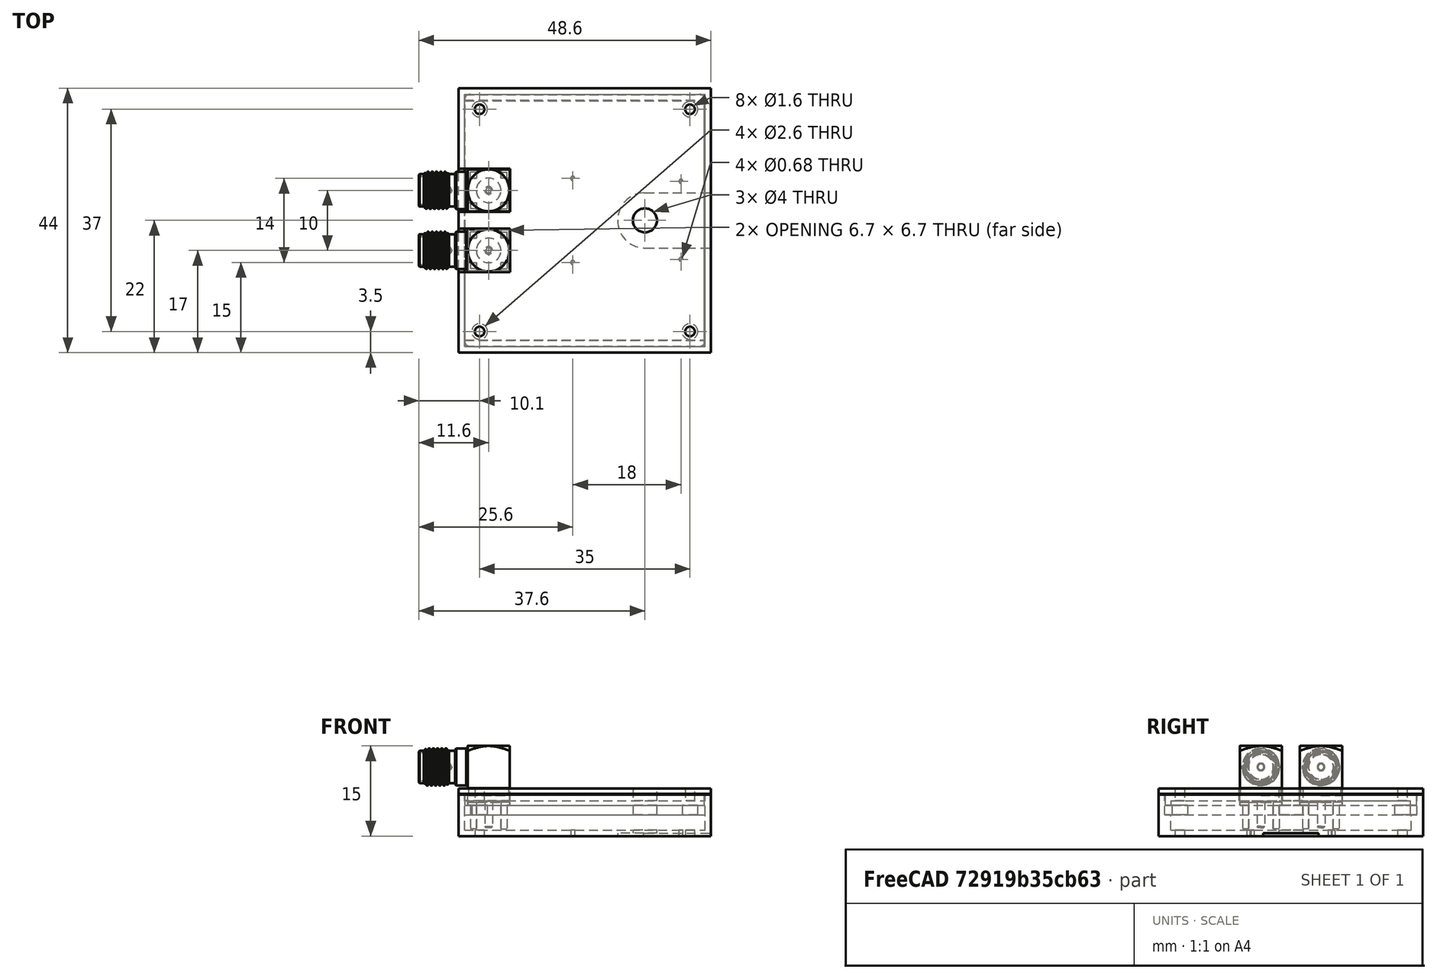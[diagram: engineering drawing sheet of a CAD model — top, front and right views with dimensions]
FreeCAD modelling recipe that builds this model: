
FCSTD DOCUMENT  (FreeCAD 0.21R33675 (Git))
Label: ModulationKickerHousing
License: All rights reserved
LicenseURL: http://en.wikipedia.org/wiki/All_rights_reserved
objects: TechDraw::DrawViewDimension×52, Part::Cylinder×21, Part::Box×12, Part::Cut×11, TechDraw::DrawProjGroupItem×9, Part::Compound×8, Part::MultiFuse×4, TechDraw::DrawSVGTemplate×3, TechDraw::DrawProjGroup×3, TechDraw::DrawPage×3, Part::Feature×2, TechDraw::DrawViewSection×2, App::Link×1, Part::Fillet×1
note: 151 computed .brp shape members not serialized (recipe doc carries the construction recipe); baked Part::Feature solids carry a one-line shape summary decoded from their .brp
EXTERNAL_REF file=../../PhilipsXL30/XL30FinalAppertureHolder.FCStd obj=Cut001_solid

FEATURE [Part::Box] Box  label="Würfel"
  AttacherType = Attacher::AttachEngine3D
  Height = 1.6
  Length = 40
  Width = 42
FEATURE [Part::Feature] Solid  label="901-143-6RFX"
  Placement = pos=(0,0,0) rot=(-1,0,0;1.5708rad)
  shape: bbox 16.55 x 9.9 x 13.8 mm, 108 faces (baked)
FEATURE [Part::Compound] Compound
  Links = -> [Solid]
  Placement = pos=(4,16,8) rot=(0,0,1;3.14159rad)
FEATURE [Part::Cylinder] Cylinder  label="Zylinder"
  Angle = 360
  AttacherType = Attacher::AttachEngine3D
  FirstAngle = 0
  Height = 5
  Placement = pos=(30,21,0) rot=(0,0,1;0rad)
  Radius = 2
  SecondAngle = 0
FEATURE [Part::Cut] Cut
  Base = -> Box
  Tool = -> Cylinder
FEATURE [Part::Box] Box001  label="Würfel001"
  AttacherType = Attacher::AttachEngine3D
  Height = 7
  Length = 42
  Placement = pos=(-1,-1,-4.4) rot=(0,0,1;0rad)
  Width = 44
FEATURE [Part::Box] Box002  label="Würfel002"
  AttacherType = Attacher::AttachEngine3D
  Height = 6
  Length = 40
  Placement = pos=(0,0,-3.4) rot=(0,0,1;0rad)
  Width = 42
FEATURE [Part::Cut] Cut001
  Base = -> Box001
  Tool = -> Box002
FEATURE [Part::Cylinder] Cylinder001  label="Zylinder001"
  Angle = 360
  AttacherType = Attacher::AttachEngine3D
  FirstAngle = 0
  Height = 20
  Placement = pos=(30,21,-10) rot=(0,0,1;0rad)
  Radius = 2
  SecondAngle = 0
FEATURE [Part::Cut] Cut002
  Base = -> Cut001
  Tool = -> Cylinder001
FEATURE [Part::Box] Box003  label="Würfel003"
  AttacherType = Attacher::AttachEngine3D
  Height = 2.5
  Length = 40
  Placement = pos=(0,0,-3.4) rot=(0,0,1;0rad)
  Width = 1
FEATURE [Part::Box] Box004  label="Würfel004"
  AttacherType = Attacher::AttachEngine3D
  Height = 2.5
  Length = 40
  Placement = pos=(0,41,-3.4) rot=(0,0,1;0rad)
  Width = 1
FEATURE [Part::MultiFuse] Fusion
  Shapes = -> [Box003,Box004,Cut002]
FEATURE [Part::Box] Box005  label="Würfel005"
  AttacherType = Attacher::AttachEngine3D
  Height = 1
  Length = 39.8
  Placement = pos=(0.1,0.1,1.5) rot=(0,0,1;0rad)
  Width = 41.8
FEATURE [Part::Box] Box006  label="Würfel006"
  AttacherType = Attacher::AttachEngine3D
  Height = 1
  Length = 42
  Placement = pos=(-1,-1,2.5) rot=(0,0,1;0rad)
  Width = 44
FEATURE [Part::MultiFuse] Fusion001
  Shapes = -> [Box005,Box006]
FEATURE [Part::Box] Box007  label="Würfel007"
  AttacherType = Attacher::AttachEngine3D
  Height = 10
  Length = 20
  Placement = pos=(-12.4,12.4,0) rot=(0,0,1;0rad)
  Width = 7.2
FEATURE [Part::Cut] Cut003
  Base = -> Fusion001
  Tool = -> Box007
FEATURE [Part::Box] Box008  label="Würfel008"
  AttacherType = Attacher::AttachEngine3D
  Height = 0.5
  Length = 18
  Placement = pos=(27.5,16.4,-4.4) rot=(0,0,1;0rad)
  Width = 9.2
FEATURE [Part::Cylinder] Cylinder002  label="Zylinder002"
  Angle = 360
  AttacherType = Attacher::AttachEngine3D
  FirstAngle = 0
  Height = 0.5
  Placement = pos=(27.75,21,-4.4) rot=(0,0,1;0rad)
  Radius = 4.6
  SecondAngle = 0
FEATURE [Part::Cylinder] Cylinder003  label="Zylinder003"
  Angle = 360
  AttacherType = Attacher::AttachEngine3D
  FirstAngle = 0
  Height = 0.5
  Placement = pos=(27.75,21,-4.4) rot=(0,0,1;0rad)
  Radius = 4.6
  SecondAngle = 0
FEATURE [Part::MultiFuse] Fusion002
  Placement = pos=(2.3,0,0) rot=(0,0,1;0rad)
  Shapes = -> [Box008,Cylinder002,Cylinder003]
FEATURE [Part::Cut] Cut004
  Base = -> Fusion
  Tool = -> Fusion002
FEATURE [Part::Cylinder] Cylinder004  label="Zylinder004"
  Angle = 360
  AttacherType = Attacher::AttachEngine3D
  FirstAngle = 0
  Height = 100
  Placement = pos=(18,14,-50) rot=(0,0,1;0rad)
  Radius = 0.34
  SecondAngle = 0
FEATURE [Part::Cylinder] Cylinder005  label="Zylinder005"
  Angle = 360
  AttacherType = Attacher::AttachEngine3D
  FirstAngle = 0
  Height = 100
  Placement = pos=(18,28,-50) rot=(0,0,1;0rad)
  Radius = 0.34
  SecondAngle = 0
FEATURE [Part::Cylinder] Cylinder006  label="Zylinder006"
  Angle = 360
  AttacherType = Attacher::AttachEngine3D
  FirstAngle = 0
  Height = 100
  Placement = pos=(36,14.5,-50) rot=(0,0,1;0rad)
  Radius = 0.34
  SecondAngle = 0
FEATURE [Part::Cylinder] Cylinder007  label="Zylinder007"
  Angle = 360
  AttacherType = Attacher::AttachEngine3D
  FirstAngle = 0
  Height = 100
  Placement = pos=(36,27.5,-50) rot=(0,0,1;0rad)
  Radius = 0.34
  SecondAngle = 0
FEATURE [Part::Compound] Compound002  label="M1TapHoles"
  Links = -> [Cylinder004,Cylinder005,Cylinder006,Cylinder007]
FEATURE [Part::Cut] Cut005
  Base = -> Cut004
  Tool = -> Compound002
FEATURE [Part::Box] Box009  label="Würfel009"
  AttacherType = Attacher::AttachEngine3D
  Height = 0.8
  Length = 39.8
  Placement = pos=(0.1,40.9,0.7) rot=(0,0,1;0rad)
  Width = 1
FEATURE [Part::Box] Box010  label="Würfel010"
  AttacherType = Attacher::AttachEngine3D
  Height = 0.8
  Length = 39.8
  Placement = pos=(0.1,0.1,0.7) rot=(0,0,1;0rad)
  Width = 1
FEATURE [Part::Compound] Compound003
  Links = -> [Box009,Box010]
FEATURE [Part::MultiFuse] Fusion003
  Shapes = -> [Cut003,Compound003]
FEATURE [Part::Cylinder] Cylinder008  label="Zylinder008"
  Angle = 360
  AttacherType = Attacher::AttachEngine3D
  FirstAngle = 0
  Height = 20
  Placement = pos=(37.5,2.5,-10) rot=(0,0,1;0rad)
  Radius = 0.8
  SecondAngle = 0
FEATURE [Part::Cylinder] Cylinder009  label="Zylinder009"
  Angle = 360
  AttacherType = Attacher::AttachEngine3D
  FirstAngle = 0
  Height = 20
  Placement = pos=(2.5,2.5,-10) rot=(0,0,1;0rad)
  Radius = 0.8
  SecondAngle = 0
FEATURE [Part::Cylinder] Cylinder010  label="Zylinder010"
  Angle = 360
  AttacherType = Attacher::AttachEngine3D
  FirstAngle = 0
  Height = 20
  Placement = pos=(37.5,39.5,-10) rot=(0,0,1;0rad)
  Radius = 0.8
  SecondAngle = 0
FEATURE [Part::Cylinder] Cylinder011  label="Zylinder011"
  Angle = 360
  AttacherType = Attacher::AttachEngine3D
  FirstAngle = 0
  Height = 20
  Placement = pos=(2.5,39.5,-10) rot=(0,0,1;0rad)
  Radius = 0.8
  SecondAngle = 0
FEATURE [Part::Cylinder] Cylinder012  label="Zylinder012"
  Angle = 360
  AttacherType = Attacher::AttachEngine3D
  FirstAngle = 0
  Height = 20
  Placement = pos=(37.5,2.5,-10) rot=(0,0,1;0rad)
  Radius = 1.3
  SecondAngle = 0
FEATURE [Part::Cylinder] Cylinder013  label="Zylinder013"
  Angle = 360
  AttacherType = Attacher::AttachEngine3D
  FirstAngle = 0
  Height = 20
  Placement = pos=(2.5,2.5,-10) rot=(0,0,1;0rad)
  Radius = 1.3
  SecondAngle = 0
FEATURE [Part::Cylinder] Cylinder014  label="Zylinder014"
  Angle = 360
  AttacherType = Attacher::AttachEngine3D
  FirstAngle = 0
  Height = 20
  Placement = pos=(37.5,39.5,-10) rot=(0,0,1;0rad)
  Radius = 1.3
  SecondAngle = 0
FEATURE [Part::Cylinder] Cylinder015  label="Zylinder015"
  Angle = 360
  AttacherType = Attacher::AttachEngine3D
  FirstAngle = 0
  Height = 20
  Placement = pos=(2.5,39.5,-10) rot=(0,0,1;0rad)
  Radius = 1.3
  SecondAngle = 0
FEATURE [Part::Compound] Compound004
  Links = -> [Cylinder015,Cylinder012,Cylinder013,Cylinder014]
FEATURE [Part::Cylinder] Cylinder016  label="Zylinder016"
  Angle = 360
  AttacherType = Attacher::AttachEngine3D
  FirstAngle = 0
  Height = 20
  Placement = pos=(37.5,2.5,-10) rot=(0,0,1;0rad)
  Radius = 0.8
  SecondAngle = 0
FEATURE [Part::Cylinder] Cylinder017  label="Zylinder017"
  Angle = 360
  AttacherType = Attacher::AttachEngine3D
  FirstAngle = 0
  Height = 20
  Placement = pos=(2.5,2.5,-10) rot=(0,0,1;0rad)
  Radius = 0.8
  SecondAngle = 0
FEATURE [Part::Cylinder] Cylinder018  label="Zylinder018"
  Angle = 360
  AttacherType = Attacher::AttachEngine3D
  FirstAngle = 0
  Height = 20
  Placement = pos=(37.5,39.5,-10) rot=(0,0,1;0rad)
  Radius = 0.8
  SecondAngle = 0
FEATURE [Part::Cylinder] Cylinder019  label="Zylinder019"
  Angle = 360
  AttacherType = Attacher::AttachEngine3D
  FirstAngle = 0
  Height = 20
  Placement = pos=(2.5,39.5,-10) rot=(0,0,1;0rad)
  Radius = 0.8
  SecondAngle = 0
FEATURE [Part::Compound] Compound005
  Links = -> [Cylinder008,Cylinder009,Cylinder010,Cylinder011]
FEATURE [Part::Cut] Cut007  label="UpperPart"
  Base = -> Cut005
  Tool = -> Compound005
FEATURE [Part::Compound] Compound006
  Links = -> [Cylinder019,Cylinder016,Cylinder017,Cylinder018]
FEATURE [Part::Cut] Cut008  label="LowerPart"
  Base = -> Fusion003
  Tool = -> Compound006
FEATURE [App::Link] Link  label="XL30FinalAppertureHolder"
  LinkPlacement = pos=(30,21,-4) rot=(1,0,0;3.14159rad)
  LinkedObject = -> <external ../../PhilipsXL30/XL30FinalAppertureHolder.FCStd>#Cut001_solid
  Placement = pos=(30,21,-4) rot=(1,0,0;3.14159rad)
FEATURE [TechDraw::DrawSVGTemplate] Template
  EditableTexts = Designed_by_Name=Thomas Spielauer; FC-Date=2023-10-02; FC-SC=mm; FC-SH=1/3; FC-Title=SemKicker Housing v2; Subtitle=Version 2, Lower Part, Dual Port
  Height = 210
  Orientation = 1
  Template = <path>
  Width = 297
FEATURE [TechDraw::DrawProjGroupItem] ProjItem  label="Front"
  CoarseView = false
  Direction = (0,0,-1)
  Focus = 100
  HardHidden = false
  IsoCount = 0
  IsoHidden = false
  IsoVisible = false
  LockPosition = true
  Perspective = false
  Rotation = 0
  RotationVector = (0,1,0)
  ScaleType = 2
  ScrubCount = 0
  SeamHidden = false
  SeamVisible = false
  SmoothHidden = false
  SmoothVisible = true
  Source = -> [Cut007]
  Type = 0
  X = 0
  XDirection = (0,1,0)
  Y = 0
FEATURE [TechDraw::DrawProjGroupItem] ProjItem001  label="Left"
  CoarseView = false
  Direction = (0,-1,-1e-16)
  Focus = 100
  HardHidden = false
  IsoCount = 0
  IsoHidden = false
  IsoVisible = false
  LockPosition = false
  Perspective = false
  Rotation = 0
  RotationVector = (1,0,0)
  ScaleType = 2
  ScrubCount = 0
  SeamHidden = false
  SeamVisible = false
  SmoothHidden = false
  SmoothVisible = true
  Source = -> [Cut007]
  Type = 1
  X = 55.0312
  XDirection = (0,1e-16,-1)
  Y = 0
FEATURE [TechDraw::DrawProjGroupItem] ProjItem002  label="Top"
  CoarseView = false
  Direction = (1,0,0)
  Focus = 100
  HardHidden = false
  IsoCount = 0
  IsoHidden = false
  IsoVisible = false
  LockPosition = false
  Perspective = false
  Rotation = 0
  RotationVector = (1,0,0)
  ScaleType = 2
  ScrubCount = 0
  SeamHidden = false
  SeamVisible = false
  SmoothHidden = false
  SmoothVisible = true
  Source = -> [Cut007]
  Type = 4
  X = 0
  XDirection = (0,1,0)
  Y = -63.5568
FEATURE [TechDraw::DrawProjGroupItem] ProjItem003  label="FrontTopLeft"
  CoarseView = false
  Direction = (0.57735,-0.57735,-0.57735)
  Focus = 100
  HardHidden = false
  IsoCount = 0
  IsoHidden = false
  IsoVisible = false
  LockPosition = false
  Perspective = false
  Rotation = 0
  RotationVector = (1,0,0)
  ScaleType = 2
  ScrubCount = 0
  SeamHidden = false
  SeamVisible = false
  SmoothHidden = false
  SmoothVisible = true
  Source = -> [Cut007]
  Type = 6
  X = 55.0312
  XDirection = (0,0.707107,-0.707107)
  Y = -63.5568
FEATURE [TechDraw::DrawProjGroup] ProjGroup
  Anchor = -> ProjItem
  AutoDistribute = true
  LockPosition = false
  ProjectionType = 0
  Rotation = 0
  ScaleType = 0
  Source = -> [Cut007]
  Views = -> [ProjItem,ProjItem001,ProjItem002,ProjItem003]
  X = 55.1699
  Y = 140.445
  spacingX = 15
  spacingY = 15
FEATURE [TechDraw::DrawViewDimension] Dimension
  AngleOverride = false
  Arbitrary = false
  ArbitraryTolerances = false
  EqualTolerance = true
  ExtensionAngle = 0
  FormatSpec = %.2w
  FormatSpecOverTolerance = %+.2w
  FormatSpecUnderTolerance = %+.2w
  Inverted = false
  LineAngle = 0
  LockPosition = false
  MeasureType = 1
  OverTolerance = 0
  References2D = -> [ProjItem]
  Rotation = 0
  ScaleType = 0
  TheoreticalExact = false
  Type = 1
  UnderTolerance = 0
  X = 1.25393
  Y = -36.4347
FEATURE [TechDraw::DrawViewDimension] Dimension001
  AngleOverride = false
  Arbitrary = false
  ArbitraryTolerances = false
  EqualTolerance = true
  ExtensionAngle = 0
  FormatSpec = %.2w
  FormatSpecOverTolerance = %+.2w
  FormatSpecUnderTolerance = %+.2w
  Inverted = false
  LineAngle = 0
  LockPosition = false
  MeasureType = 1
  OverTolerance = 0
  References2D = -> [ProjItem]
  Rotation = 0
  ScaleType = 0
  TheoreticalExact = false
  Type = 1
  UnderTolerance = 0
  X = -0.666797
  Y = 33.2207
FEATURE [TechDraw::DrawViewDimension] Dimension002
  AngleOverride = false
  Arbitrary = false
  ArbitraryTolerances = false
  EqualTolerance = true
  ExtensionAngle = 0
  FormatSpec = ⌀%.2w
  FormatSpecOverTolerance = %+.2w
  FormatSpecUnderTolerance = %+.2w
  Inverted = false
  LineAngle = 0
  LockPosition = false
  MeasureType = 1
  OverTolerance = 0
  References2D = -> [ProjItem]
  Rotation = 0
  ScaleType = 0
  TheoreticalExact = false
  Type = 5
  UnderTolerance = 0
  X = 28.4277
  Y = 10.052
FEATURE [TechDraw::DrawViewDimension] Dimension003
  AngleOverride = false
  Arbitrary = false
  ArbitraryTolerances = false
  EqualTolerance = true
  ExtensionAngle = 0
  FormatSpec = %.2w
  FormatSpecOverTolerance = %+.2w
  FormatSpecUnderTolerance = %+.2w
  Inverted = false
  LineAngle = 0
  LockPosition = false
  MeasureType = 1
  OverTolerance = 0
  References2D = -> [ProjItem]
  Rotation = 0
  ScaleType = 0
  TheoreticalExact = false
  Type = 1
  UnderTolerance = 0
  X = -29.3827
  Y = 33.2539
FEATURE [TechDraw::DrawViewDimension] Dimension004
  AngleOverride = false
  Arbitrary = false
  ArbitraryTolerances = false
  EqualTolerance = true
  ExtensionAngle = 0
  FormatSpec = %.2w
  FormatSpecOverTolerance = %+.2w
  FormatSpecUnderTolerance = %+.2w
  Inverted = false
  LineAngle = 0
  LockPosition = false
  MeasureType = 1
  OverTolerance = 0
  References2D = -> [ProjItem]
  Rotation = 0
  ScaleType = 0
  TheoreticalExact = false
  Type = 0
  UnderTolerance = 0
  X = 20.6616
  Y = 33.2266
FEATURE [TechDraw::DrawViewDimension] Dimension005
  AngleOverride = false
  Arbitrary = false
  ArbitraryTolerances = false
  EqualTolerance = true
  ExtensionAngle = 0
  FormatSpec = %.2w
  FormatSpecOverTolerance = %+.2w
  FormatSpecUnderTolerance = %+.2w
  Inverted = false
  LineAngle = 0
  LockPosition = false
  MeasureType = 1
  OverTolerance = 0
  References2D = -> [ProjItem]
  Rotation = 0
  ScaleType = 0
  TheoreticalExact = false
  Type = 2
  UnderTolerance = 0
  X = -39.0583
  Y = 14.7874
FEATURE [TechDraw::DrawViewDimension] Dimension006
  AngleOverride = false
  Arbitrary = false
  ArbitraryTolerances = false
  EqualTolerance = true
  ExtensionAngle = 0
  FormatSpec = %.2w
  FormatSpecOverTolerance = %+.2w
  FormatSpecUnderTolerance = %+.2w
  Inverted = false
  LineAngle = 0
  LockPosition = false
  MeasureType = 1
  OverTolerance = 0
  References2D = -> [ProjItem]
  Rotation = 0
  ScaleType = 0
  TheoreticalExact = false
  Type = 1
  UnderTolerance = 0
  X = -15.1318
  Y = 48.9061
FEATURE [TechDraw::DrawViewDimension] Dimension007
  AngleOverride = false
  Arbitrary = false
  ArbitraryTolerances = false
  EqualTolerance = true
  ExtensionAngle = 0
  FormatSpec = %.2w
  FormatSpecOverTolerance = %+.2w
  FormatSpecUnderTolerance = %+.2w
  Inverted = false
  LineAngle = 0
  LockPosition = false
  MeasureType = 1
  OverTolerance = 0
  References2D = -> [ProjItem]
  Rotation = 0
  ScaleType = 0
  TheoreticalExact = false
  Type = 1
  UnderTolerance = 0
  X = 13.258
  Y = 44.6428
FEATURE [TechDraw::DrawViewDimension] Dimension008
  AngleOverride = false
  Arbitrary = false
  ArbitraryTolerances = false
  EqualTolerance = true
  ExtensionAngle = 0
  FormatSpec = %.2w
  FormatSpecOverTolerance = %+.2w
  FormatSpecUnderTolerance = %+.2w
  Inverted = false
  LineAngle = 0
  LockPosition = false
  MeasureType = 1
  OverTolerance = 0
  References2D = -> [ProjItem]
  Rotation = 0
  ScaleType = 0
  TheoreticalExact = false
  Type = 2
  UnderTolerance = 0
  X = 29.2563
  Y = 26.6245
FEATURE [TechDraw::DrawViewDimension] Dimension009
  AngleOverride = false
  Arbitrary = false
  ArbitraryTolerances = false
  EqualTolerance = true
  ExtensionAngle = 0
  FormatSpec = ⌀%.2w (4x M2)
  FormatSpecOverTolerance = %+.2w
  FormatSpecUnderTolerance = %+.2w
  Inverted = false
  LineAngle = 0
  LockPosition = false
  MeasureType = 1
  OverTolerance = 0
  References2D = -> [ProjItem]
  Rotation = 0
  ScaleType = 0
  TheoreticalExact = false
  Type = 5
  UnderTolerance = 0
  X = 60.575
  Y = 34.3091
FEATURE [TechDraw::DrawViewDimension] Dimension010
  AngleOverride = false
  Arbitrary = false
  ArbitraryTolerances = false
  EqualTolerance = true
  ExtensionAngle = 0
  FormatSpec = %.2w
  FormatSpecOverTolerance = %+.2w
  FormatSpecUnderTolerance = %+.2w
  Inverted = false
  LineAngle = 0
  LockPosition = false
  MeasureType = 1
  OverTolerance = 0
  References2D = -> [ProjItem]
  Rotation = 0
  ScaleType = 0
  TheoreticalExact = false
  Type = 2
  UnderTolerance = 0
  X = -33.5126
  Y = 2.06556
FEATURE [TechDraw::DrawViewDimension] Dimension011
  AngleOverride = false
  Arbitrary = false
  ArbitraryTolerances = false
  EqualTolerance = true
  ExtensionAngle = 0
  FormatSpec = %.2w
  FormatSpecOverTolerance = %+.2w
  FormatSpecUnderTolerance = %+.2w
  Inverted = false
  LineAngle = 0
  LockPosition = false
  MeasureType = 1
  OverTolerance = 0
  References2D = -> [ProjItem]
  Rotation = 0
  ScaleType = 0
  TheoreticalExact = false
  Type = 2
  UnderTolerance = 0
  X = 27.8187
  Y = -8.37147
FEATURE [TechDraw::DrawViewDimension] Dimension012
  AngleOverride = false
  Arbitrary = false
  ArbitraryTolerances = false
  EqualTolerance = true
  ExtensionAngle = 0
  FormatSpec = %.2w
  FormatSpecOverTolerance = %+.2w
  FormatSpecUnderTolerance = %+.2w
  Inverted = false
  LineAngle = 0
  LockPosition = false
  MeasureType = 1
  OverTolerance = 0
  References2D = -> [ProjItem]
  Rotation = 0
  ScaleType = 0
  TheoreticalExact = false
  Type = 2
  UnderTolerance = 0
  X = 45.3481
  Y = -9.26073
FEATURE [TechDraw::DrawViewDimension] Dimension013
  AngleOverride = false
  Arbitrary = false
  ArbitraryTolerances = false
  EqualTolerance = true
  ExtensionAngle = 0
  FormatSpec = %.2w
  FormatSpecOverTolerance = %+.2w
  FormatSpecUnderTolerance = %+.2w
  Inverted = false
  LineAngle = 0
  LockPosition = false
  MeasureType = 1
  OverTolerance = 0
  References2D = -> [ProjItem]
  Rotation = 0
  ScaleType = 0
  TheoreticalExact = false
  Type = 1
  UnderTolerance = 0
  X = 35.7665
  Y = -22.6841
FEATURE [TechDraw::DrawViewDimension] Dimension014
  AngleOverride = false
  Arbitrary = false
  ArbitraryTolerances = false
  EqualTolerance = true
  ExtensionAngle = 0
  FormatSpec = %.2w
  FormatSpecOverTolerance = %+.2w
  FormatSpecUnderTolerance = %+.2w
  Inverted = false
  LineAngle = 0
  LockPosition = false
  MeasureType = 1
  OverTolerance = 0
  References2D = -> [ProjItem]
  Rotation = 0
  ScaleType = 0
  TheoreticalExact = false
  Type = 1
  UnderTolerance = 0
  X = 9.78618
  Y = -21.3047
FEATURE [TechDraw::DrawViewDimension] Dimension015
  AngleOverride = false
  Arbitrary = false
  ArbitraryTolerances = false
  EqualTolerance = true
  ExtensionAngle = 0
  FormatSpec = %.2w
  FormatSpecOverTolerance = %+.2w
  FormatSpecUnderTolerance = %+.2w
  Inverted = false
  LineAngle = 0
  LockPosition = false
  MeasureType = 1
  OverTolerance = 0
  References2D = -> [ProjItem001]
  Rotation = 0
  ScaleType = 0
  TheoreticalExact = false
  Type = 1
  UnderTolerance = 0
  X = 8.50538
  Y = 32.6804
FEATURE [TechDraw::DrawViewDimension] Dimension016
  AngleOverride = false
  Arbitrary = false
  ArbitraryTolerances = false
  EqualTolerance = true
  ExtensionAngle = 0
  FormatSpec = %.2w
  FormatSpecOverTolerance = %+.2w
  FormatSpecUnderTolerance = %+.2w
  Inverted = false
  LineAngle = 0
  LockPosition = false
  MeasureType = 1
  OverTolerance = 0
  References2D = -> [ProjItem002]
  Rotation = 0
  ScaleType = 0
  TheoreticalExact = false
  Type = 2
  UnderTolerance = 0
  X = -33.4894
  Y = 14.4313
FEATURE [TechDraw::DrawViewDimension] Dimension017
  AngleOverride = false
  Arbitrary = false
  ArbitraryTolerances = false
  EqualTolerance = true
  ExtensionAngle = 0
  FormatSpec = %.2w
  FormatSpecOverTolerance = %+.2w
  FormatSpecUnderTolerance = %+.2w
  Inverted = false
  LineAngle = 0
  LockPosition = false
  MeasureType = 1
  OverTolerance = 0
  References2D = -> [ProjItem002]
  Rotation = 0
  ScaleType = 0
  TheoreticalExact = false
  Type = 2
  UnderTolerance = 0
  X = 22.4587
  Y = -6.89394
FEATURE [TechDraw::DrawPage] Page
  KeepUpdated = true
  NextBalloonIndex = 1
  ProjectionType = 0
  Template = -> Template
  Views = -> [ProjGroup,Dimension,Dimension001,Dimension002,Dimension003,Dimension004,Dimension005,Dimension006,Dimension007,Dimension008,Dimension009,Dimension010,Dimension011,Dimension012,Dimension013,Dimension014,Dimension015,Dimension016,Dimension017]
FEATURE [TechDraw::DrawSVGTemplate] Template001
  EditableTexts = Designed_by_Name=Thomas Spielauer; FC-Date=2023-10-02; FC-SC=mm; FC-SH=2/3; FC-Title=SemKicker Housing v2; Subtitle=Version 2, Lower Part, Dual Port
  Height = 210
  Orientation = 1
  Template = <path>
  Width = 297
FEATURE [TechDraw::DrawProjGroupItem] ProjItem004  label="Front001"
  CoarseView = false
  Direction = (0,0,-1)
  Focus = 100
  HardHidden = false
  IsoCount = 0
  IsoHidden = false
  IsoVisible = false
  LockPosition = true
  Perspective = false
  Rotation = 0
  RotationVector = (0,1,0)
  ScaleType = 2
  ScrubCount = 0
  SeamHidden = false
  SeamVisible = false
  SmoothHidden = false
  SmoothVisible = true
  Source = -> [Cut007]
  Type = 0
  X = 0
  XDirection = (0,1,0)
  Y = 0
FEATURE [TechDraw::DrawProjGroup] ProjGroup001
  Anchor = -> ProjItem004
  AutoDistribute = true
  LockPosition = false
  ProjectionType = 0
  Rotation = 0
  ScaleType = 0
  Source = -> [Cut007]
  Views = -> [ProjItem004]
  X = 67.5139
  Y = 171.126
  spacingX = 15
  spacingY = 15
FEATURE [TechDraw::DrawViewSection] SectionView  label="Section  - "
  BaseView = -> ProjItem004
  CoarseView = false
  CutSurfaceDisplay = 2
  Direction = (1,1e-16,0)
  FileGeomPattern = <path>
  FileHatchPattern = <path>
  Focus = 100
  FuseBeforeCut = false
  HardHidden = false
  HatchOffset = (0,0,0)
  HatchRotation = 0
  HatchScale = 1
  IsoCount = 0
  IsoHidden = false
  IsoVisible = false
  LockPosition = false
  NameGeomPattern = Diamant
  Perspective = false
  Rotation = 0
  Scale = 5
  ScaleType = 1
  ScrubCount = 0
  SeamHidden = false
  SeamVisible = false
  SectionDirection = 4
  SectionNormal = (1,1e-16,0)
  SectionOrigin = (20,21,-0.9)
  SmoothHidden = false
  SmoothVisible = true
  Source = -> [Cut007]
  TrimAfterCut = false
  X = 152.009
  XDirection = (-1e-16,1,0)
  Y = 85.8328
FEATURE [TechDraw::DrawViewDimension] Dimension018
  AngleOverride = false
  Arbitrary = false
  ArbitraryTolerances = false
  EqualTolerance = true
  ExtensionAngle = 0
  FormatSpec = %.2w
  FormatSpecOverTolerance = %+.2w
  FormatSpecUnderTolerance = %+.2w
  Inverted = false
  LineAngle = 0
  LockPosition = false
  MeasureType = 1
  OverTolerance = 0
  References2D = -> [SectionView]
  Rotation = 0
  ScaleType = 0
  TheoreticalExact = false
  Type = 0
  UnderTolerance = 0
  X = 4.24631
  Y = 33.9522
FEATURE [TechDraw::DrawViewDimension] Dimension019
  AngleOverride = false
  Arbitrary = false
  ArbitraryTolerances = false
  EqualTolerance = true
  ExtensionAngle = 0
  FormatSpec = %.2w
  FormatSpecOverTolerance = %+.2w
  FormatSpecUnderTolerance = %+.2w
  Inverted = false
  LineAngle = 0
  LockPosition = false
  MeasureType = 1
  OverTolerance = 0
  References2D = -> [SectionView]
  Rotation = 0
  ScaleType = 0
  TheoreticalExact = false
  Type = 1
  UnderTolerance = 0
  X = 4.11387
  Y = 41.9407
FEATURE [TechDraw::DrawViewDimension] Dimension020
  AngleOverride = false
  Arbitrary = false
  ArbitraryTolerances = false
  EqualTolerance = true
  ExtensionAngle = 0
  FormatSpec = %.2w
  FormatSpecOverTolerance = %+.2w
  FormatSpecUnderTolerance = %+.2w
  Inverted = false
  LineAngle = 0
  LockPosition = false
  MeasureType = 1
  OverTolerance = 0
  References2D = -> [SectionView]
  Rotation = 0
  ScaleType = 0
  TheoreticalExact = false
  Type = 1
  UnderTolerance = 0
  X = 3.83962
  Y = 50.2209
FEATURE [TechDraw::DrawViewDimension] Dimension021
  AngleOverride = false
  Arbitrary = false
  ArbitraryTolerances = false
  EqualTolerance = true
  ExtensionAngle = 0
  FormatSpec = %.2w
  FormatSpecOverTolerance = %+.2w
  FormatSpecUnderTolerance = %+.2w
  Inverted = false
  LineAngle = 0
  LockPosition = false
  MeasureType = 1
  OverTolerance = 0
  References2D = -> [SectionView]
  Rotation = 0
  ScaleType = 0
  TheoreticalExact = false
  Type = 2
  UnderTolerance = 0
  X = -118.97
  Y = 14.3399
FEATURE [TechDraw::DrawViewDimension] Dimension022
  AngleOverride = false
  Arbitrary = false
  ArbitraryTolerances = false
  EqualTolerance = true
  ExtensionAngle = 0
  FormatSpec = %.2w
  FormatSpecOverTolerance = %+.2w
  FormatSpecUnderTolerance = %+.2w
  Inverted = false
  LineAngle = 0
  LockPosition = false
  MeasureType = 1
  OverTolerance = 0
  References2D = -> [SectionView]
  Rotation = 0
  ScaleType = 0
  TheoreticalExact = false
  Type = 2
  UnderTolerance = 0
  X = -127.962
  Y = 12.8645
FEATURE [TechDraw::DrawViewDimension] Dimension023
  AngleOverride = false
  Arbitrary = false
  ArbitraryTolerances = false
  EqualTolerance = true
  ExtensionAngle = 0
  FormatSpec = %.2w
  FormatSpecOverTolerance = %+.2w
  FormatSpecUnderTolerance = %+.2w
  Inverted = false
  LineAngle = 0
  LockPosition = false
  MeasureType = 1
  OverTolerance = 0
  References2D = -> [SectionView]
  Rotation = 0
  ScaleType = 0
  TheoreticalExact = false
  Type = 2
  UnderTolerance = 0
  X = -127.985
  Y = -3.21183
FEATURE [TechDraw::DrawViewDimension] Dimension024
  AngleOverride = false
  Arbitrary = false
  ArbitraryTolerances = false
  EqualTolerance = true
  ExtensionAngle = 0
  FormatSpec = ⌀%.2w (4x M1)
  FormatSpecOverTolerance = %+.2w
  FormatSpecUnderTolerance = %+.2w
  Inverted = false
  LineAngle = 0
  LockPosition = false
  MeasureType = 1
  OverTolerance = 0
  References2D = -> [ProjItem004]
  Rotation = 0
  ScaleType = 0
  TheoreticalExact = false
  Type = 5
  UnderTolerance = 0
  X = 58.9306
  Y = -8.01169
FEATURE [TechDraw::DrawViewSection] SectionView001  label="Section  - 001"
  BaseView = -> ProjItem004
  CoarseView = false
  CutSurfaceDisplay = 2
  Direction = (-1e-16,-1,0)
  FileGeomPattern = <path>
  FileHatchPattern = <path>
  Focus = 100
  FuseBeforeCut = false
  HardHidden = false
  HatchOffset = (0,0,0)
  HatchRotation = 0
  HatchScale = 1
  IsoCount = 0
  IsoHidden = false
  IsoVisible = false
  LockPosition = false
  NameGeomPattern = Diamant
  Perspective = false
  Rotation = -90
  ScaleType = 2
  ScrubCount = 0
  SeamHidden = false
  SeamVisible = false
  SectionDirection = 4
  SectionNormal = (-1e-16,-1,0)
  SectionOrigin = (17,21,-0.9)
  SmoothHidden = false
  SmoothVisible = true
  Source = -> [Cut007]
  TrimAfterCut = false
  X = 189.424
  XDirection = (-1,1e-16,0)
  Y = 161.061
FEATURE [TechDraw::DrawViewDimension] Dimension025
  AngleOverride = false
  Arbitrary = false
  ArbitraryTolerances = false
  EqualTolerance = true
  ExtensionAngle = 0
  FormatSpec = %.2w
  FormatSpecOverTolerance = %+.2w
  FormatSpecUnderTolerance = %+.2w
  Inverted = false
  LineAngle = 0
  LockPosition = false
  MeasureType = 1
  OverTolerance = 0
  References2D = -> [SectionView001]
  Rotation = 0
  ScaleType = 0
  TheoreticalExact = false
  Type = 2
  UnderTolerance = 0
  X = -12.7324
  Y = 3.6305
FEATURE [TechDraw::DrawViewDimension] Dimension026
  AngleOverride = false
  Arbitrary = false
  ArbitraryTolerances = false
  EqualTolerance = true
  ExtensionAngle = 0
  FormatSpec = %.2w
  FormatSpecOverTolerance = %+.2w
  FormatSpecUnderTolerance = %+.2w
  Inverted = false
  LineAngle = 0
  LockPosition = false
  MeasureType = 1
  OverTolerance = 0
  References2D = -> [SectionView001]
  Rotation = 0
  ScaleType = 0
  TheoreticalExact = false
  Type = 2
  UnderTolerance = 0
  X = 10.8197
  Y = 1.93475
FEATURE [TechDraw::DrawViewDimension] Dimension027
  AngleOverride = false
  Arbitrary = false
  ArbitraryTolerances = false
  EqualTolerance = true
  ExtensionAngle = 0
  FormatSpec = %.2w
  FormatSpecOverTolerance = %+.2w
  FormatSpecUnderTolerance = %+.2w
  Inverted = false
  LineAngle = 0
  LockPosition = false
  MeasureType = 1
  OverTolerance = 0
  References2D = -> [SectionView001]
  Rotation = 0
  ScaleType = 0
  TheoreticalExact = false
  Type = 1
  UnderTolerance = 0
  X = 10.4362
  Y = 32.1751
FEATURE [TechDraw::DrawViewDimension] Dimension028
  AngleOverride = false
  Arbitrary = false
  ArbitraryTolerances = false
  EqualTolerance = true
  ExtensionAngle = 0
  FormatSpec = %.2w
  FormatSpecOverTolerance = %+.2w
  FormatSpecUnderTolerance = %+.2w
  Inverted = false
  LineAngle = 0
  LockPosition = false
  MeasureType = 1
  OverTolerance = 0
  References2D = -> [SectionView001]
  Rotation = 0
  ScaleType = 0
  TheoreticalExact = false
  Type = 1
  UnderTolerance = 0
  X = -1.2953
  Y = 37.9733
FEATURE [TechDraw::DrawPage] Page001
  KeepUpdated = true
  NextBalloonIndex = 1
  ProjectionType = 0
  Template = -> Template001
  Views = -> [ProjGroup001,SectionView,Dimension018,Dimension019,Dimension020,Dimension021,Dimension022,Dimension023,Dimension024,SectionView001,Dimension025,Dimension026,Dimension027,Dimension028]
FEATURE [Part::Feature] Part__Feature  label="901-143-6RFX001"
  Placement = pos=(0,0,0) rot=(1,0,0;-1.5708rad)
  shape: bbox 16.55 x 9.9 x 13.8 mm, 108 faces (baked)
FEATURE [Part::Compound] Compound007
  Links = -> [Part__Feature]
  Placement = pos=(4,26,8) rot=(0,0,1;3.14159rad)
FEATURE [Part::Compound] Compound001  label="PCB"
  Links = -> [Cut,Compound,Compound007]
  Placement = pos=(0,0,-0.9) rot=(0,0,1;0rad)
FEATURE [Part::Fillet] Fillet  label="PCBRound"
  Base = -> Compound001
  Edges = 4 edges r=1: [Edge1,Edge3,Edge6,Edge12]
FEATURE [Part::Cut] Cut006  label="PCBWithHoles"
  Base = -> Fillet
  Tool = -> Compound004
FEATURE [Part::Box] Box011  label="Würfel011"
  AttacherType = Attacher::AttachEngine3D
  Height = 10
  Length = 20
  Placement = pos=(-12.4,22.4,0) rot=(0,0,1;0rad)
  Width = 7.2
FEATURE [Part::Cut] Cut009  label="LowerPart2"
  Base = -> Cut008
  Tool = -> Box011
FEATURE [TechDraw::DrawSVGTemplate] Template002
  EditableTexts = Designed_by_Name=Thomas Spielauer; FC-Date=2023-10-05; FC-SC=mm; FC-SH=3/3; FC-Title=SemKicker Housing v2; Subtitle=Version 2, Upper Part, Dual Port
  Height = 210
  Orientation = 1
  Template = <path>
  Width = 297
FEATURE [TechDraw::DrawProjGroupItem] ProjItem005  label="Front002"
  CoarseView = false
  Direction = (0,0,1)
  Focus = 100
  HardHidden = false
  IsoCount = 0
  IsoHidden = false
  IsoVisible = false
  LockPosition = true
  Perspective = false
  Rotation = 0
  RotationVector = (0,-1,0)
  ScaleType = 2
  ScrubCount = 0
  SeamHidden = false
  SeamVisible = false
  SmoothHidden = false
  SmoothVisible = true
  Source = -> [Cut009]
  Type = 0
  X = 0
  XDirection = (0,-1,0)
  Y = 0
FEATURE [TechDraw::DrawProjGroupItem] ProjItem006  label="Rear"
  CoarseView = false
  Direction = (0,0,-1)
  Focus = 100
  HardHidden = false
  IsoCount = 0
  IsoHidden = false
  IsoVisible = false
  LockPosition = false
  Perspective = false
  Rotation = 0
  RotationVector = (1,0,0)
  ScaleType = 2
  ScrubCount = 0
  SeamHidden = false
  SeamVisible = false
  SmoothHidden = false
  SmoothVisible = true
  Source = -> [Cut009]
  Type = 3
  X = 76.8
  XDirection = (0,1,0)
  Y = 0
FEATURE [TechDraw::DrawProjGroupItem] ProjItem007  label="Left001"
  CoarseView = false
  Direction = (0,1,1e-16)
  Focus = 100
  HardHidden = false
  IsoCount = 0
  IsoHidden = false
  IsoVisible = false
  LockPosition = false
  Perspective = false
  Rotation = 0
  RotationVector = (1,0,0)
  ScaleType = 2
  ScrubCount = 0
  SeamHidden = false
  SeamVisible = false
  SmoothHidden = false
  SmoothVisible = true
  Source = -> [Cut009]
  Type = 1
  X = 38.4
  XDirection = (0,-1e-16,1)
  Y = 0
FEATURE [TechDraw::DrawProjGroupItem] ProjItem008  label="Bottom"
  CoarseView = false
  Direction = (-1,0,0)
  Focus = 100
  HardHidden = false
  IsoCount = 0
  IsoHidden = false
  IsoVisible = false
  LockPosition = false
  Perspective = false
  Rotation = 0
  RotationVector = (1,0,0)
  ScaleType = 2
  ScrubCount = 0
  SeamHidden = false
  SeamVisible = false
  SmoothHidden = false
  SmoothVisible = true
  Source = -> [Cut009]
  Type = 5
  X = 0
  XDirection = (0,-1,0)
  Y = 37.4
FEATURE [TechDraw::DrawProjGroup] ProjGroup002
  Anchor = -> ProjItem005
  AutoDistribute = true
  LockPosition = false
  ProjectionType = 0
  Rotation = 0
  ScaleType = 0
  Source = -> [Cut009]
  Views = -> [ProjItem005,ProjItem006,ProjItem007,ProjItem008]
  X = 66.9874
  Y = 111.502
  spacingX = 15
  spacingY = 15
FEATURE [TechDraw::DrawViewDimension] Dimension029
  AngleOverride = false
  Arbitrary = false
  ArbitraryTolerances = false
  EqualTolerance = true
  ExtensionAngle = 0
  FormatSpec = %.2w
  FormatSpecOverTolerance = %+.2w
  FormatSpecUnderTolerance = %+.2w
  Inverted = false
  LineAngle = 0
  LockPosition = false
  MeasureType = 1
  OverTolerance = 0
  References2D = -> [ProjItem005]
  Rotation = 0
  ScaleType = 0
  TheoreticalExact = false
  Type = 0
  UnderTolerance = 0
  X = 1.32648
  Y = -43.1876
FEATURE [TechDraw::DrawViewDimension] Dimension030
  AngleOverride = false
  Arbitrary = false
  ArbitraryTolerances = false
  EqualTolerance = true
  ExtensionAngle = 0
  FormatSpec = %.2w
  FormatSpecOverTolerance = %+.2w
  FormatSpecUnderTolerance = %+.2w
  Inverted = false
  LineAngle = 0
  LockPosition = false
  MeasureType = 1
  OverTolerance = 0
  References2D = -> [ProjItem005]
  Rotation = 0
  ScaleType = 0
  TheoreticalExact = false
  Type = 2
  UnderTolerance = 0
  X = -40.3534
  Y = 4.02495
FEATURE [TechDraw::DrawViewDimension] Dimension031
  AngleOverride = false
  Arbitrary = false
  ArbitraryTolerances = false
  EqualTolerance = true
  ExtensionAngle = 0
  FormatSpec = %.2w
  FormatSpecOverTolerance = %+.2w
  FormatSpecUnderTolerance = %+.2w
  Inverted = false
  LineAngle = 0
  LockPosition = false
  MeasureType = 1
  OverTolerance = 0
  References2D = -> [ProjItem005]
  Rotation = 0
  ScaleType = 0
  TheoreticalExact = false
  Type = 0
  UnderTolerance = 0
  X = 2.27138
  Y = 3.23613
FEATURE [TechDraw::DrawViewDimension] Dimension032
  AngleOverride = false
  Arbitrary = false
  ArbitraryTolerances = false
  EqualTolerance = true
  ExtensionAngle = 0
  FormatSpec = %.2w
  FormatSpecOverTolerance = %+.2w
  FormatSpecUnderTolerance = %+.2w
  Inverted = false
  LineAngle = 0
  LockPosition = false
  MeasureType = 1
  OverTolerance = 0
  References2D = -> [ProjItem005]
  Rotation = 0
  ScaleType = 0
  TheoreticalExact = false
  Type = 1
  UnderTolerance = 0
  X = -15.2702
  Y = -35.1551
FEATURE [TechDraw::DrawViewDimension] Dimension033
  AngleOverride = false
  Arbitrary = false
  ArbitraryTolerances = false
  EqualTolerance = true
  ExtensionAngle = 0
  FormatSpec = %.2w
  FormatSpecOverTolerance = %+.2w
  FormatSpecUnderTolerance = %+.2w
  Inverted = false
  LineAngle = 0
  LockPosition = false
  MeasureType = 1
  OverTolerance = 0
  References2D = -> [ProjItem005]
  Rotation = 0
  ScaleType = 0
  TheoreticalExact = false
  Type = 0
  UnderTolerance = 0
  X = 6.21091
  Y = -34.953
FEATURE [TechDraw::DrawViewDimension] Dimension034
  AngleOverride = false
  Arbitrary = false
  ArbitraryTolerances = false
  EqualTolerance = true
  ExtensionAngle = 0
  FormatSpec = %.2w
  FormatSpecOverTolerance = %+.2w
  FormatSpecUnderTolerance = %+.2w
  Inverted = false
  LineAngle = 0
  LockPosition = false
  MeasureType = 1
  OverTolerance = 0
  References2D = -> [ProjItem008]
  Rotation = 0
  ScaleType = 0
  TheoreticalExact = false
  Type = 1
  UnderTolerance = 0
  X = -25.2543
  Y = -2.7081
FEATURE [TechDraw::DrawViewDimension] Dimension035
  AngleOverride = false
  Arbitrary = false
  ArbitraryTolerances = false
  EqualTolerance = true
  ExtensionAngle = 0
  FormatSpec = %.2w
  FormatSpecOverTolerance = %+.2w
  FormatSpecUnderTolerance = %+.2w
  Inverted = false
  LineAngle = 0
  LockPosition = false
  MeasureType = 1
  OverTolerance = 0
  References2D = -> [ProjItem008]
  Rotation = 0
  ScaleType = 0
  TheoreticalExact = false
  Type = 0
  UnderTolerance = 0
  X = -21.7866
  Y = 12.3693
FEATURE [TechDraw::DrawViewDimension] Dimension036
  AngleOverride = false
  Arbitrary = false
  ArbitraryTolerances = false
  EqualTolerance = true
  ExtensionAngle = 0
  FormatSpec = %.2w
  FormatSpecOverTolerance = %+.2w
  FormatSpecUnderTolerance = %+.2w
  Inverted = false
  LineAngle = 0
  LockPosition = false
  MeasureType = 1
  OverTolerance = 0
  References2D = -> [ProjItem008]
  Rotation = 0
  ScaleType = 0
  TheoreticalExact = false
  Type = 1
  UnderTolerance = 0
  X = 14.6137
  Y = 12.6016
FEATURE [TechDraw::DrawViewDimension] Dimension037
  AngleOverride = false
  Arbitrary = false
  ArbitraryTolerances = false
  EqualTolerance = true
  ExtensionAngle = 0
  FormatSpec = %.2w
  FormatSpecOverTolerance = %+.2w
  FormatSpecUnderTolerance = %+.2w
  Inverted = false
  LineAngle = 0
  LockPosition = false
  MeasureType = 1
  OverTolerance = 0
  References2D = -> [ProjItem008]
  Rotation = 0
  ScaleType = 0
  TheoreticalExact = false
  Type = 1
  UnderTolerance = 0
  X = 4.3783
  Y = 21.0728
FEATURE [TechDraw::DrawViewDimension] Dimension038
  AngleOverride = false
  Arbitrary = false
  ArbitraryTolerances = false
  EqualTolerance = true
  ExtensionAngle = 0
  FormatSpec = %.2w
  FormatSpecOverTolerance = %+.2w
  FormatSpecUnderTolerance = %+.2w
  Inverted = false
  LineAngle = 0
  LockPosition = false
  MeasureType = 1
  OverTolerance = 0
  References2D = -> [ProjItem008]
  Rotation = 0
  ScaleType = 0
  TheoreticalExact = false
  Type = 1
  UnderTolerance = 0
  X = 30.8167
  Y = 2.21089
FEATURE [TechDraw::DrawViewDimension] Dimension039
  AngleOverride = false
  Arbitrary = false
  ArbitraryTolerances = false
  EqualTolerance = true
  ExtensionAngle = 0
  FormatSpec = %.2w
  FormatSpecOverTolerance = %+.2w
  FormatSpecUnderTolerance = %+.2w
  Inverted = false
  LineAngle = 0
  LockPosition = false
  MeasureType = 1
  OverTolerance = 0
  References2D = -> [ProjItem005]
  Rotation = 0
  ScaleType = 0
  TheoreticalExact = false
  Type = 0
  UnderTolerance = 0
  X = -31.4858
  Y = -23.4358
FEATURE [TechDraw::DrawViewDimension] Dimension040
  AngleOverride = false
  Arbitrary = false
  ArbitraryTolerances = false
  EqualTolerance = true
  ExtensionAngle = 0
  FormatSpec = %.2w
  FormatSpecOverTolerance = %+.2w
  FormatSpecUnderTolerance = %+.2w
  Inverted = false
  LineAngle = 0
  LockPosition = false
  MeasureType = 1
  OverTolerance = 0
  References2D = -> [ProjItem005]
  Rotation = 0
  ScaleType = 0
  TheoreticalExact = false
  Type = 0
  UnderTolerance = 0
  X = -50.4808
  Y = -16.0474
FEATURE [TechDraw::DrawViewDimension] Dimension041
  AngleOverride = false
  Arbitrary = false
  ArbitraryTolerances = false
  EqualTolerance = true
  ExtensionAngle = 0
  FormatSpec = ⌀%.2w
  FormatSpecOverTolerance = %+.2w
  FormatSpecUnderTolerance = %+.2w
  Inverted = false
  LineAngle = 0
  LockPosition = false
  MeasureType = 1
  OverTolerance = 0
  References2D = -> [ProjItem005]
  Rotation = 0
  ScaleType = 0
  TheoreticalExact = false
  Type = 5
  UnderTolerance = 0
  X = 33.6425
  Y = -39.7092
FEATURE [TechDraw::DrawViewDimension] Dimension042
  AngleOverride = false
  Arbitrary = false
  ArbitraryTolerances = false
  EqualTolerance = true
  ExtensionAngle = 0
  FormatSpec = %.2w
  FormatSpecOverTolerance = %+.2w
  FormatSpecUnderTolerance = %+.2w
  Inverted = false
  LineAngle = 0
  LockPosition = false
  MeasureType = 1
  OverTolerance = 0
  References2D = -> [ProjItem006]
  Rotation = 0
  ScaleType = 0
  TheoreticalExact = false
  Type = 2
  UnderTolerance = 0
  X = 37.644
  Y = -2.88729
FEATURE [TechDraw::DrawViewDimension] Dimension043
  AngleOverride = false
  Arbitrary = false
  ArbitraryTolerances = false
  EqualTolerance = true
  ExtensionAngle = 0
  FormatSpec = %.2w
  FormatSpecOverTolerance = %+.2w
  FormatSpecUnderTolerance = %+.2w
  Inverted = false
  LineAngle = 0
  LockPosition = false
  MeasureType = 1
  OverTolerance = 0
  References2D = -> [ProjItem006]
  Rotation = 0
  ScaleType = 0
  TheoreticalExact = false
  Type = 1
  UnderTolerance = 0
  X = 25.8121
  Y = -34.2488
FEATURE [TechDraw::DrawViewDimension] Dimension044
  AngleOverride = false
  Arbitrary = false
  ArbitraryTolerances = false
  EqualTolerance = true
  ExtensionAngle = 0
  FormatSpec = %.2w
  FormatSpecOverTolerance = %+.2w
  FormatSpecUnderTolerance = %+.2w
  Inverted = false
  LineAngle = 0
  LockPosition = false
  MeasureType = 1
  OverTolerance = 0
  References2D = -> [ProjItem006]
  Rotation = 0
  ScaleType = 0
  TheoreticalExact = false
  Type = 1
  UnderTolerance = 0
  X = -22.4115
  Y = -31.9364
FEATURE [TechDraw::DrawViewDimension] Dimension045
  AngleOverride = false
  Arbitrary = false
  ArbitraryTolerances = false
  EqualTolerance = true
  ExtensionAngle = 0
  FormatSpec = %.2w
  FormatSpecOverTolerance = %+.2w
  FormatSpecUnderTolerance = %+.2w
  Inverted = false
  LineAngle = 0
  LockPosition = false
  MeasureType = 1
  OverTolerance = 0
  References2D = -> [ProjItem006]
  Rotation = 0
  ScaleType = 0
  TheoreticalExact = false
  Type = 1
  UnderTolerance = 0
  X = 5.98519
  Y = 1.50775
FEATURE [TechDraw::DrawViewDimension] Dimension046
  AngleOverride = false
  Arbitrary = false
  ArbitraryTolerances = false
  EqualTolerance = true
  ExtensionAngle = 0
  FormatSpec = %.2w
  FormatSpecOverTolerance = %+.2w
  FormatSpecUnderTolerance = %+.2w
  Inverted = false
  LineAngle = 0
  LockPosition = false
  MeasureType = 1
  OverTolerance = 0
  References2D = -> [ProjItem006]
  Rotation = 0
  ScaleType = 0
  TheoreticalExact = false
  Type = 2
  UnderTolerance = 0
  X = -36.1328
  Y = 33.5742
FEATURE [TechDraw::DrawViewDimension] Dimension047
  AngleOverride = false
  Arbitrary = false
  ArbitraryTolerances = false
  EqualTolerance = true
  ExtensionAngle = 0
  FormatSpec = %.2w
  FormatSpecOverTolerance = %+.2w
  FormatSpecUnderTolerance = %+.2w
  Inverted = false
  LineAngle = 0
  LockPosition = false
  MeasureType = 1
  OverTolerance = 0
  References2D = -> [ProjItem006]
  Rotation = 0
  ScaleType = 0
  TheoreticalExact = false
  Type = 2
  UnderTolerance = 0
  X = 53.1193
  Y = 30.7597
FEATURE [TechDraw::DrawViewDimension] Dimension048
  AngleOverride = false
  Arbitrary = false
  ArbitraryTolerances = false
  EqualTolerance = true
  ExtensionAngle = 0
  FormatSpec = %.2w
  FormatSpecOverTolerance = %+.2w
  FormatSpecUnderTolerance = %+.2w
  Inverted = false
  LineAngle = 0
  LockPosition = false
  MeasureType = 1
  OverTolerance = 0
  References2D = -> [ProjItem006]
  Rotation = 0
  ScaleType = 0
  TheoreticalExact = false
  Type = 1
  UnderTolerance = 0
  X = 32.2346
  Y = 45.4319
FEATURE [TechDraw::DrawViewDimension] Dimension049
  AngleOverride = false
  Arbitrary = false
  ArbitraryTolerances = false
  EqualTolerance = true
  ExtensionAngle = 0
  FormatSpec = %.2w
  FormatSpecOverTolerance = %+.2w
  FormatSpecUnderTolerance = %+.2w
  Inverted = false
  LineAngle = 0
  LockPosition = false
  MeasureType = 1
  OverTolerance = 0
  References2D = -> [ProjItem007]
  Rotation = 0
  ScaleType = 0
  TheoreticalExact = false
  Type = 1
  UnderTolerance = 0
  X = -10.7258
  Y = 43.5922
FEATURE [TechDraw::DrawViewDimension] Dimension050
  AngleOverride = false
  Arbitrary = false
  ArbitraryTolerances = false
  EqualTolerance = true
  ExtensionAngle = 0
  FormatSpec = %.2w
  FormatSpecOverTolerance = %+.2w
  FormatSpecUnderTolerance = %+.2w
  Inverted = false
  LineAngle = 0
  LockPosition = false
  MeasureType = 1
  OverTolerance = 0
  References2D = -> [ProjItem007]
  Rotation = 0
  ScaleType = 0
  TheoreticalExact = false
  Type = 1
  UnderTolerance = 0
  X = 6.714
  Y = -16.8889
FEATURE [TechDraw::DrawViewDimension] Dimension051
  AngleOverride = false
  Arbitrary = false
  ArbitraryTolerances = false
  EqualTolerance = true
  ExtensionAngle = 0
  FormatSpec = %.2w
  FormatSpecOverTolerance = %+.2w
  FormatSpecUnderTolerance = %+.2w
  Inverted = false
  LineAngle = 0
  LockPosition = false
  MeasureType = 1
  OverTolerance = 0
  References2D = -> [ProjItem008]
  Rotation = 0
  ScaleType = 0
  TheoreticalExact = false
  Type = 1
  UnderTolerance = 0
  X = 30.7564
  Y = -5.25465
FEATURE [TechDraw::DrawPage] Page002
  KeepUpdated = true
  NextBalloonIndex = 1
  ProjectionType = 0
  Template = -> Template002
  Views = -> [ProjGroup002,Dimension029,Dimension030,Dimension031,Dimension032,Dimension033,Dimension034,Dimension035,Dimension036,Dimension037,Dimension038,Dimension039,Dimension040,Dimension041,Dimension042,Dimension043,Dimension044,Dimension045,Dimension046,Dimension047,Dimension048,Dimension049,Dimension050,Dimension051]
FEATURE [Part::Cylinder] Cylinder020  label="Zylinder020"
  Angle = 360
  AttacherType = Attacher::AttachEngine3D
  FirstAngle = 0
  Height = 100
  Placement = pos=(30,21,-50) rot=(0,0,1;0rad)
  Radius = 2
  SecondAngle = 0
FEATURE [Part::Cut] Cut010  label="LowerPartHole"
  Base = -> Cut009
  Tool = -> Cylinder020
note: 7 file-system paths scrubbed to <path> (originals preserved in the JSON sidecar)
